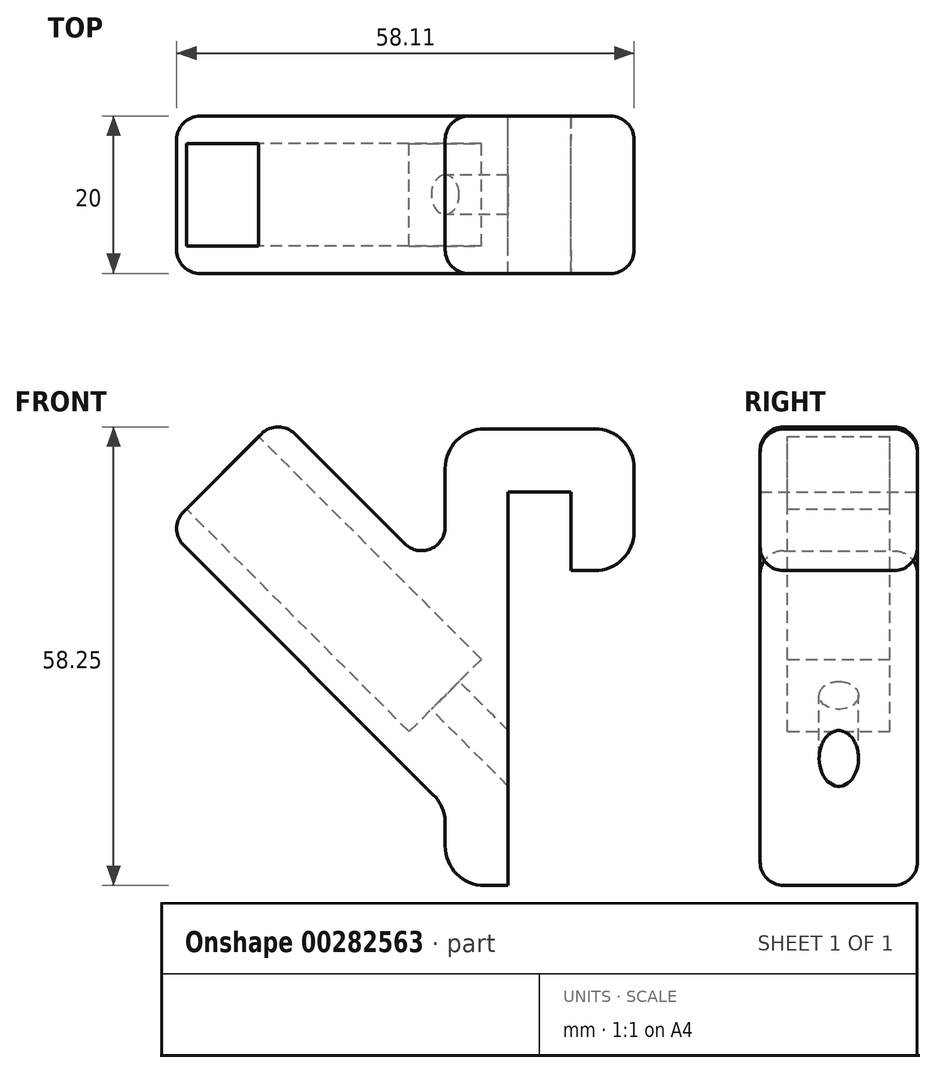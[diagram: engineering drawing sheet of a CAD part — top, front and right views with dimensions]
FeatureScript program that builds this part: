
annotation { "Feature Type Name" : "Feature", "Feature Type Description" : "" }
export const myFeature = defineFeature(function(context is Context, id is Id, definition is map)
    precondition{}
    {
        {
            var Q0;
            Q0=qCreatedBy(makeId("Front.planeOp"),FACE);
            var sketch = newSketch(context, id + "F0", { "sketchPlane" : qUnion([Q0])});
            skLineSegment(sketch, "E0", {"start": v(0, 0) * mm, "end": v(0, 10) * mm});
            skLineSegment(sketch, "E1", {"start": v(0, 10) * mm, "end": v(-8, 10) * mm});
            skLineSegment(sketch, "E2", {"start": v(-8, 10) * mm, "end": v(-8, -40) * mm});
            skLineSegment(sketch, "E3", {"start": v(-49.23, 7.48) * mm, "end": v(-39.33, 17.38) * mm});
            skLineSegment(sketch, "E4", {"start": v(-35.1, 17.38) * mm, "end": v(-21.12, 3.4) * mm});
            skLineSegment(sketch, "E5", {"start": v(-16, 5.53) * mm, "end": v(-16, 13) * mm});
            skLineSegment(sketch, "E6", {"start": v(-11, 18) * mm, "end": v(3, 18) * mm});
            skLineSegment(sketch, "E7", {"start": v(8, 13) * mm, "end": v(8, 5) * mm});
            skLineSegment(sketch, "E8", {"start": v(3, 0) * mm, "end": v(0, 0) * mm});
            skLineSegment(sketch, "E9", {"start": v(-47.82, 8.9) * mm, "end": v(-19.54, -19.4) * mm, "construction": true});
            skLineSegment(sketch, "E10", {"start": v(-19.54, -19.4) * mm, "end": v(-12.46, -12.32) * mm, "construction": true});
            skLineSegment(sketch, "E11", {"start": v(-12.46, -12.32) * mm, "end": v(-40.75, 15.96) * mm, "construction": true});
            skLineSegment(sketch, "E12", {"start": v(-8, -40) * mm, "end": v(-11, -40) * mm});
            skLineSegment(sketch, "E13", {"start": v(-16, -35) * mm, "end": v(-16, -32.07) * mm});
            skLineSegment(sketch, "E14", {"start": v(-17.46, -28.54) * mm, "end": v(-49.23, 3.23) * mm});
            skPoint(sketch, "E15.visualSharp", {"position": v(-16, 18) * mm});
            skArc(sketch, "E15.filletArc", {"start": v(-11, 18) * mm, "mid": v(-14.54, 16.54) * mm, "end": v(-16, 13) * mm});
            skPoint(sketch, "E16.visualSharp", {"position": v(8, 18) * mm});
            skArc(sketch, "E16.filletArc", {"start": v(8, 13) * mm, "mid": v(6.54, 16.54) * mm, "end": v(3, 18) * mm});
            skPoint(sketch, "E17.visualSharp", {"position": v(-16, -40) * mm});
            skArc(sketch, "E17.filletArc", {"start": v(-16, -35) * mm, "mid": v(-14.54, -38.54) * mm, "end": v(-11, -40) * mm});
            skPoint(sketch, "E18.visualSharp", {"position": v(8, 0) * mm});
            skArc(sketch, "E18.filletArc", {"start": v(3, 0) * mm, "mid": v(6.54, 1.46) * mm, "end": v(8, 5) * mm});
            skPoint(sketch, "E19.visualSharp", {"position": v(-16, -1.72) * mm});
            skArc(sketch, "E19.filletArc", {"start": v(-21.12, 3.4) * mm, "mid": v(-17.85, 2.76) * mm, "end": v(-16, 5.53) * mm});
            skPoint(sketch, "E20.visualSharp", {"position": v(-16, -30) * mm});
            skArc(sketch, "E20.filletArc", {"start": v(-16, -32.07) * mm, "mid": v(-16.38, -30.16) * mm, "end": v(-17.46, -28.54) * mm});
            skPoint(sketch, "E21.visualSharp", {"position": v(-37.21, 19.5) * mm});
            skArc(sketch, "E21.filletArc", {"start": v(-35.1, 17.38) * mm, "mid": v(-37.21, 18.25) * mm, "end": v(-39.33, 17.38) * mm});
            skPoint(sketch, "E22.visualSharp", {"position": v(-51.36, 5.36) * mm});
            skArc(sketch, "E22.filletArc", {"start": v(-49.23, 7.48) * mm, "mid": v(-50.11, 5.36) * mm, "end": v(-49.23, 3.23) * mm});
            skSolve(sketch);
        }
        {
            var Q0;
            Q0=makeQuery(id+"F0.imprint","IMPRINT",FACE,{"disambiguationData":[TD([[makeQuery(id+"F0.imprint","IMPRINT",EDGE,{"derivedFrom":sQuery(id+"F0.wireOp",EDGE,"E0")}),-1.0]])]});
            extrude(context, id + "F1", {"entities" : qUnion([Q0]), "depth" : 20 * mm});
        }
        {
            var Q0;
            Q0=makeQuery(id+"F1.opExtrude","SWEPT_FACE",FACE,{"disambiguationData":[OSD([sQuery(id+"F0.wireOp",EDGE,"E3")])]});
            var sketch = newSketch(context, id + "F2", { "sketchPlane" : qUnion([Q0])});
            skPoint(sketch, "E23", {"position": v(10, -22.53) * mm});
            skPoint(sketch, "E23.positionSnap0", {"position": v(20, -22.53) * mm});
            skPoint(sketch, "E23.positionSnap1", {"position": v(10, -15.53) * mm});
            skLineSegment(sketch, "E24.bottom", {"start": v(16.5, -29.03) * mm, "end": v(3.5, -29.03) * mm});
            skLineSegment(sketch, "E24.top", {"start": v(16.5, -16.03) * mm, "end": v(3.5, -16.03) * mm});
            skLineSegment(sketch, "E24.left", {"start": v(16.5, -29.03) * mm, "end": v(16.5, -16.03) * mm});
            skLineSegment(sketch, "E24.right", {"start": v(3.5, -29.03) * mm, "end": v(3.5, -16.03) * mm});
            skSolve(sketch);
        }
        {
            var Q0;
            Q0=makeQuery(id+"F2.imprint","IMPRINT",FACE,{"disambiguationData":[TD([[makeQuery(id+"F2.imprint","IMPRINT",EDGE,{"derivedFrom":sQuery(id+"F2.wireOp",EDGE,"E24.bottom")}),-1.0]])]});
            extrude(context, id + "F3", {"entities" : qUnion([Q0]), "operationType" : NewBodyOperationType.REMOVE, "oppositeDirection" : true, "depth" : 40 * mm});
        }
        {
            var Q0;
            Q0=makeQuery(id+"F3.boolean.opBoolean","COPY",FACE,{"derivedFrom":makeQuery(id+"F3.opExtrude","CAP_FACE",FACE,{"disambiguationData":[OSD([sQuery(id+"F2.wireOp",EDGE,"E24.bottom"),sQuery(id+"F2.wireOp",EDGE,"E24.top"),sQuery(id+"F2.wireOp",EDGE,"E24.left"),sQuery(id+"F2.wireOp",EDGE,"E24.right")])],"isStart":false})});
            var sketch = newSketch(context, id + "F4", { "sketchPlane" : qUnion([Q0])});
            skPoint(sketch, "E25", {"position": v(10, -22.53) * mm});
            skPoint(sketch, "E25.positionSnap0", {"position": v(16.5, -22.53) * mm});
            skPoint(sketch, "E25.positionSnap1", {"position": v(10, -16.03) * mm});
            skCircle(sketch, "E26", {"center": v(10, -22.53) * mm, "radius": 2.5 * mm});
            skSolve(sketch);
        }
        {
            var Q0;
            Q0=makeQuery(id+"F4.imprint","IMPRINT",FACE,{"disambiguationData":[TD([[makeQuery(id+"F4.imprint","IMPRINT",EDGE,{"derivedFrom":sQuery(id+"F4.wireOp",EDGE,"E26")}),1.0]])]});
            var Q1;
            Q1=makeQuery(id+"F1.opExtrude","SWEPT_FACE",FACE,{"disambiguationData":[OSD([sQuery(id+"F0.wireOp",EDGE,"E2")])]});
            extrude(context, id + "F5", {"entities" : qUnion([Q0]), "operationType" : NewBodyOperationType.REMOVE, "endBound" : BoundingType.UP_TO_SURFACE, "oppositeDirection" : true, "endBoundEntityFace" : qUnion([Q1]), "depth" : 25 * mm});
        }
        {
            var Q0;
            Q0=makeQuery(id+"F1.opExtrude","CAP_EDGE",EDGE,{"disambiguationData":[OSD([sQuery(id+"F0.wireOp",EDGE,"E3")])],"isStart":false});
            var Q1;
            Q1=makeQuery(id+"F1.opExtrude","CAP_EDGE",EDGE,{"disambiguationData":[OSD([sQuery(id+"F0.wireOp",EDGE,"E3")])],"isStart":true});
            fillet(context, id + "F6", {"entities" : qUnion([Q0, Q1]), "radius" : 3 * mm, "tangentPropagation" : true, "allowEdgeOverflow" : false});
        }
    });
